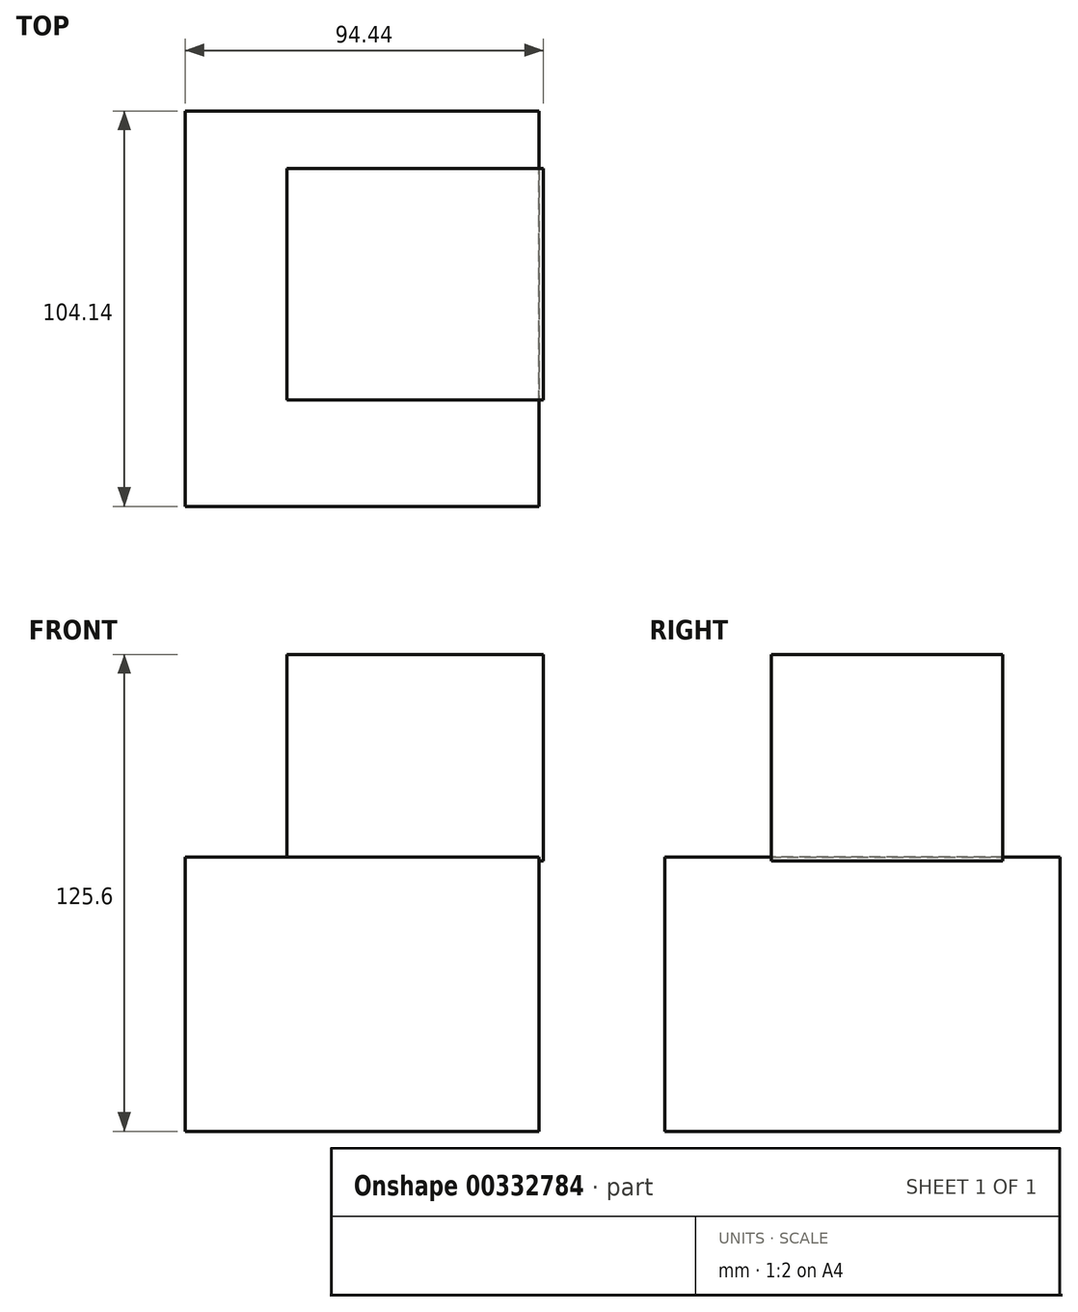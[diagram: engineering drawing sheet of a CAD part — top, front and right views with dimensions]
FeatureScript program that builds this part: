
annotation { "Feature Type Name" : "Feature", "Feature Type Description" : "" }
export const myFeature = defineFeature(function(context is Context, id is Id, definition is map)
    precondition{}
    {
        {
            var Q0;
            Q0=qCreatedBy(makeId("Front.planeOp"),FACE);
            var sketch = newSketch(context, id + "F0", { "sketchPlane" : qUnion([Q0])});
            skLineSegment(sketch, "E0.bottom", {"start": v(66.4, 23.7) * mm, "end": v(-26.88, 23.7) * mm});
            skLineSegment(sketch, "E0.top", {"start": v(66.4, -48.5) * mm, "end": v(-26.88, -48.5) * mm});
            skLineSegment(sketch, "E0.left", {"start": v(66.4, 23.7) * mm, "end": v(66.4, -48.5) * mm});
            skLineSegment(sketch, "E0.right", {"start": v(-26.88, 23.7) * mm, "end": v(-26.88, -48.5) * mm});
            skLineSegment(sketch, "E1.top", {"start": v(66.4, 0) * mm, "end": v(-26.88, 0) * mm});
            skLineSegment(sketch, "E1.left", {"start": v(66.4, 23.7) * mm, "end": v(66.4, 0) * mm});
            skLineSegment(sketch, "E1.right", {"start": v(-26.88, 23.7) * mm, "end": v(-26.88, 0) * mm});
            skSolve(sketch);
        }
        {
            var Q0;
            Q0=makeQuery(id+"F0.imprint","IMPRINT",FACE,{"disambiguationData":[TD([[makeQuery(id+"F0.imprint","IMPRINT",EDGE,{"derivedFrom":sQuery(id+"F0.wireOp",EDGE,"E0.bottom")}),1.0]])]});
            var Q1;
            Q1=makeQuery(id+"F0.imprint","IMPRINT",FACE,{"disambiguationData":[TD([[makeQuery(id+"F0.imprint","IMPRINT",EDGE,{"derivedFrom":sQuery(id+"F0.wireOp",EDGE,"E0.top")}),-1.0]])]});
            extrude(context, id + "F1", {"entities" : qUnion([Q0, Q1]), "depth" : 25.4 * mm});
        }
        {
            var Q0;
            Q0=makeQuery(id+"F1.opExtrude","CAP_FACE",FACE,{"disambiguationData":[OSD([sQuery(id+"F0.wireOp",EDGE,"E0.top"),sQuery(id+"F0.wireOp",EDGE,"E0.left"),sQuery(id+"F0.wireOp",EDGE,"E0.right"),sQuery(id+"F0.wireOp",EDGE,"E0.bottom"),sQuery(id+"F0.wireOp",EDGE,"E1.left"),sQuery(id+"F0.wireOp",EDGE,"E1.right")])],"isStart":false});
            extrude(context, id + "F2", {"entities" : qUnion([Q0]), "operationType" : NewBodyOperationType.ADD, "depth" : 78.74 * mm});
        }
        {
            var Q0;
            Q0=qCreatedBy(makeId("Right.planeOp"),FACE);
            var sketch = newSketch(context, id + "F3", { "sketchPlane" : qUnion([Q0])});
            skLineSegment(sketch, "E2.bottom", {"start": v(-76.1, 77.1) * mm, "end": v(-15.18, 77.1) * mm});
            skLineSegment(sketch, "E2.top", {"start": v(-76.1, 22.7) * mm, "end": v(-15.18, 22.7) * mm});
            skLineSegment(sketch, "E2.left", {"start": v(-76.1, 77.1) * mm, "end": v(-76.1, 22.7) * mm});
            skLineSegment(sketch, "E2.right", {"start": v(-15.18, 77.1) * mm, "end": v(-15.18, 22.7) * mm});
            skSolve(sketch);
        }
        {
            var Q0;
            Q0 = qSketchRegion(id + "F3", true);
            extrude(context, id + "F4", {"entities" : qUnion([Q0]), "operationType" : NewBodyOperationType.ADD, "depth" : 67.56 * mm});
        }
    });
